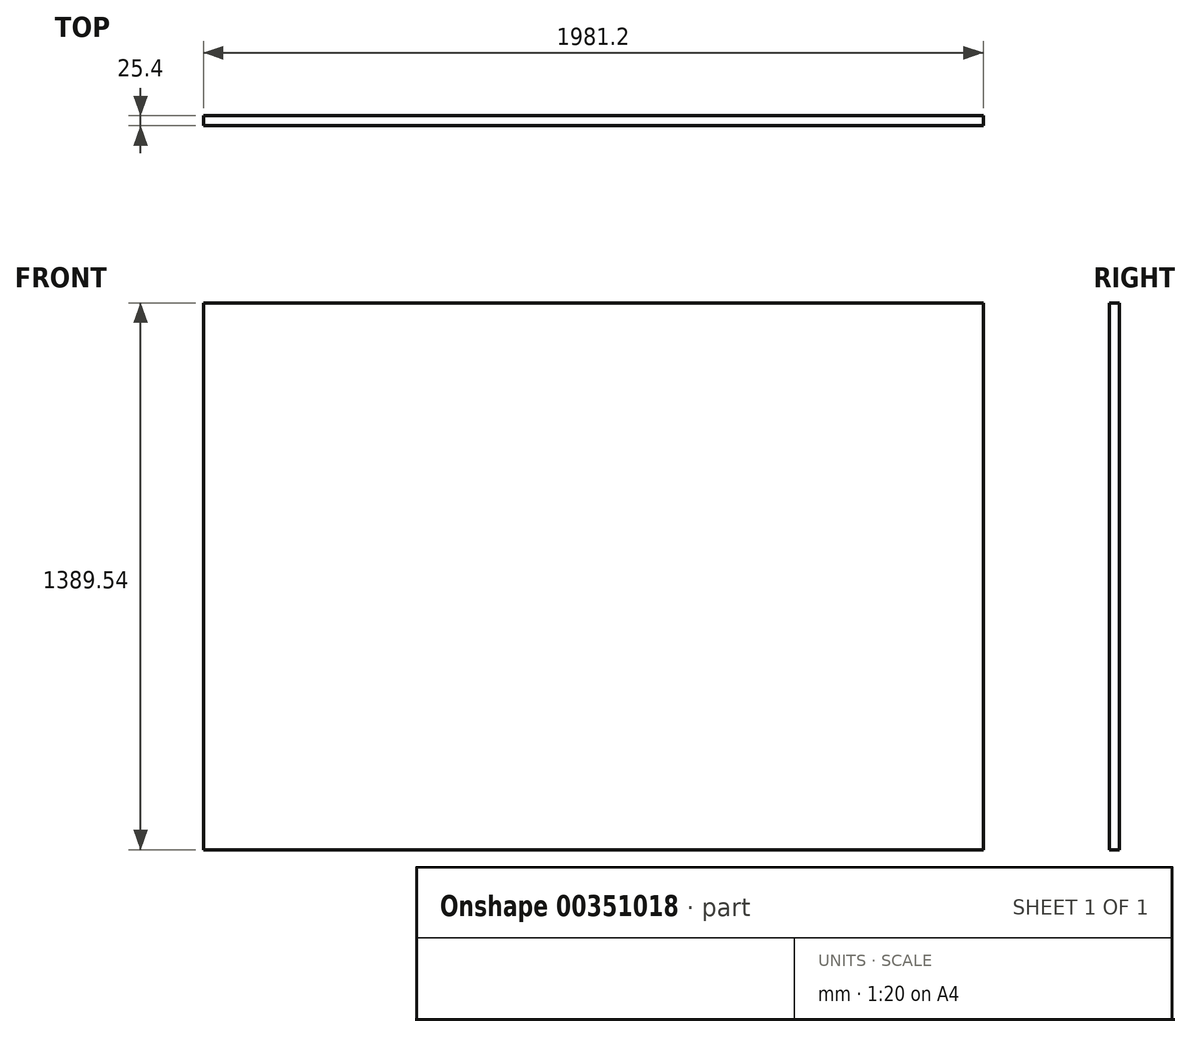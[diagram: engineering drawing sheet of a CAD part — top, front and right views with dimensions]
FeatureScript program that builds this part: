
annotation { "Feature Type Name" : "Feature", "Feature Type Description" : "" }
export const myFeature = defineFeature(function(context is Context, id is Id, definition is map)
    precondition{}
    {
        {
            var Q0;
            Q0=qCreatedBy(makeId("Front.planeOp"),FACE);
            var sketch = newSketch(context, id + "F0", { "sketchPlane" : qUnion([Q0])});
            skLineSegment(sketch, "E0.bottom", {"start": v(47.33, 0) * mm, "end": v(2028.53, 0) * mm});
            skLineSegment(sketch, "E0.top", {"start": v(47.33, 1389.54) * mm, "end": v(2028.53, 1389.54) * mm});
            skLineSegment(sketch, "E0.left", {"start": v(47.33, 0) * mm, "end": v(47.33, 1389.54) * mm});
            skLineSegment(sketch, "E0.right", {"start": v(2028.53, 0) * mm, "end": v(2028.53, 1389.54) * mm});
            skSolve(sketch);
        }
        {
            var Q0;
            Q0 = qSketchRegion(id + "F0", true);
            extrude(context, id + "F1", {"entities" : qUnion([Q0]), "depth" : 25.4 * mm});
        }
    });
